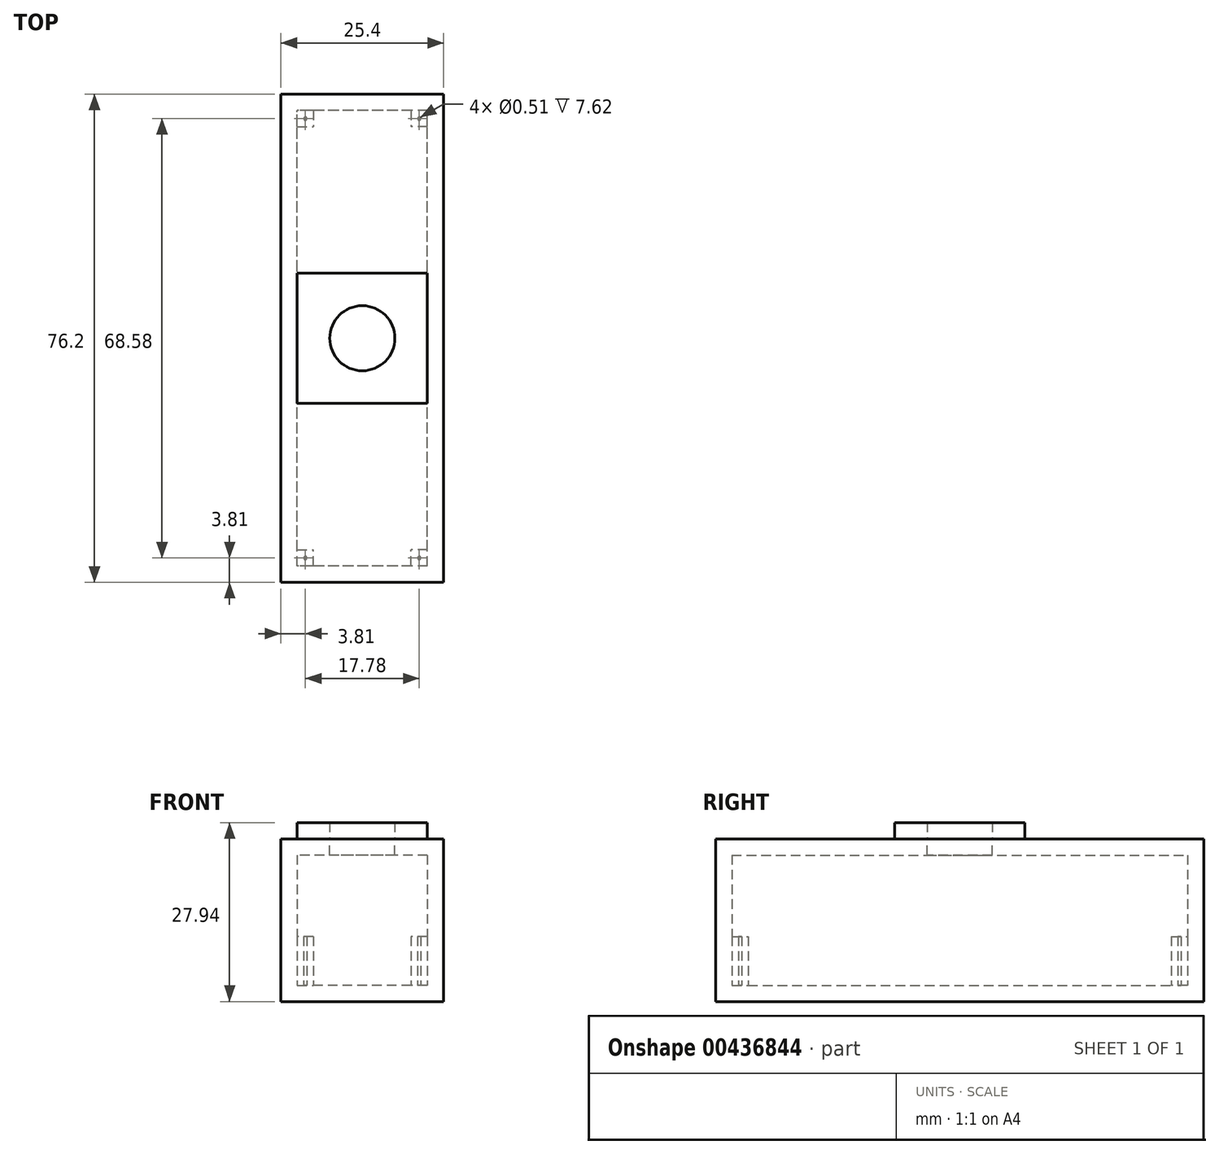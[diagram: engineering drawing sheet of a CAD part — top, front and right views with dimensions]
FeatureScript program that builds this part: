
annotation { "Feature Type Name" : "Feature", "Feature Type Description" : "" }
export const myFeature = defineFeature(function(context is Context, id is Id, definition is map)
    precondition{}
    {
        {
            var Q0;
            Q0=qCreatedBy(makeId("Front.planeOp"),FACE);
            var sketch = newSketch(context, id + "F0", { "sketchPlane" : qUnion([Q0])});
            skLineSegment(sketch, "E0.bottom", {"start": v(12.7, 12.7) * mm, "end": v(-12.7, 12.7) * mm});
            skLineSegment(sketch, "E0.top", {"start": v(12.7, -12.7) * mm, "end": v(-12.7, -12.7) * mm});
            skLineSegment(sketch, "E0.left", {"start": v(12.7, 12.7) * mm, "end": v(12.7, -12.7) * mm});
            skLineSegment(sketch, "E0.right", {"start": v(-12.7, 12.7) * mm, "end": v(-12.7, -12.7) * mm});
            skPoint(sketch, "E0.middle", {"position": v(0, 0) * mm});
            skSolve(sketch);
        }
        {
            var Q0;
            Q0=makeQuery(id+"F0.imprint","IMPRINT",FACE,{"disambiguationData":[TD([[makeQuery(id+"F0.imprint","IMPRINT",EDGE,{"derivedFrom":sQuery(id+"F0.wireOp",EDGE,"E0.bottom")}),1.0]])]});
            extrude(context, id + "F1", {"entities" : qUnion([Q0]), "endBound" : BoundingType.SYMMETRIC, "depth" : 76.2 * mm});
        }
        {
            var Q0;
            Q0=makeQuery(id+"F1.opExtrude","SWEPT_FACE",FACE,{"disambiguationData":[OSD([sQuery(id+"F0.wireOp",EDGE,"E0.right")])]});
            var Q1;
            Q1=makeQuery(id+"F1.opExtrude","SWEPT_BODY",BODY,{"disambiguationData":[OSD([sQuery(id+"F0.wireOp",EDGE,"E0.bottom"),sQuery(id+"F0.wireOp",EDGE,"E0.top"),sQuery(id+"F0.wireOp",EDGE,"E0.left"),sQuery(id+"F0.wireOp",EDGE,"E0.right")])]});
            shell(context, id + "F2", {"isHollow" : true, "entities" : qUnion([Q0]), "parts" : qUnion([Q1]), "thickness" : 2.54 * mm});
        }
        {
            var Q0;
            Q0=makeQuery(id+"F1.opExtrude","SWEPT_FACE",FACE,{"disambiguationData":[OSD([sQuery(id+"F0.wireOp",EDGE,"E0.bottom")])]});
            var sketch = newSketch(context, id + "F3", { "sketchPlane" : qUnion([Q0])});
            skLineSegment(sketch, "E1.bottom", {"start": v(10.16, 10.16) * mm, "end": v(-10.16, 10.16) * mm});
            skLineSegment(sketch, "E1.top", {"start": v(10.16, -10.16) * mm, "end": v(-10.16, -10.16) * mm});
            skLineSegment(sketch, "E1.left", {"start": v(10.16, 10.16) * mm, "end": v(10.16, -10.16) * mm});
            skLineSegment(sketch, "E1.right", {"start": v(-10.16, 10.16) * mm, "end": v(-10.16, -10.16) * mm});
            skPoint(sketch, "E1.middle", {"position": v(0, 0) * mm});
            skCircle(sketch, "E2", {"center": v(0, 0) * mm, "radius": 5.08 * mm});
            skSolve(sketch);
        }
        {
            var Q0;
            Q0=makeQuery(id+"F3.imprint","IMPRINT",FACE,{"disambiguationData":[TD([[makeQuery(id+"F3.imprint","IMPRINT",EDGE,{"derivedFrom":sQuery(id+"F3.wireOp",EDGE,"E2")}),1.0]])]});
            extrude(context, id + "F4", {"entities" : qUnion([Q0]), "operationType" : NewBodyOperationType.REMOVE, "oppositeDirection" : true, "depth" : 2.54 * mm});
        }
        {
            var Q0;
            Q0=qSketchRegion(id+"F3",true);
            extrude(context, id + "F5", {"entities" : qUnion([Q0]), "depth" : 2.54 * mm});
        }
        {
            var Q0;
            Q0=makeQuery(id+"F2.opShell","OFFSET_FACE",FACE,{"disambiguationData":[OSD([sQuery(id+"F0.wireOp",EDGE,"E0.top")])]});
            var sketch = newSketch(context, id + "F6", { "sketchPlane" : qUnion([Q0])});
            skLineSegment(sketch, "E3.bottom", {"start": v(-10.16, 35.56) * mm, "end": v(-7.62, 35.56) * mm});
            skLineSegment(sketch, "E3.top", {"start": v(-10.16, 33.02) * mm, "end": v(-7.62, 33.02) * mm});
            skLineSegment(sketch, "E3.left", {"start": v(-10.16, 35.56) * mm, "end": v(-10.16, 33.02) * mm});
            skLineSegment(sketch, "E3.right", {"start": v(-7.62, 35.56) * mm, "end": v(-7.62, 33.02) * mm});
            skLineSegment(sketch, "E4.bottom", {"start": v(10.16, 35.56) * mm, "end": v(7.62, 35.56) * mm});
            skLineSegment(sketch, "E4.top", {"start": v(10.16, 33.02) * mm, "end": v(7.62, 33.02) * mm});
            skLineSegment(sketch, "E4.left", {"start": v(10.16, 35.56) * mm, "end": v(10.16, 33.02) * mm});
            skLineSegment(sketch, "E4.right", {"start": v(7.62, 35.56) * mm, "end": v(7.62, 33.02) * mm});
            skLineSegment(sketch, "E5.bottom", {"start": v(10.16, -35.56) * mm, "end": v(7.62, -35.56) * mm});
            skLineSegment(sketch, "E5.top", {"start": v(10.16, -33.02) * mm, "end": v(7.62, -33.02) * mm});
            skLineSegment(sketch, "E5.left", {"start": v(10.16, -35.56) * mm, "end": v(10.16, -33.02) * mm});
            skLineSegment(sketch, "E5.right", {"start": v(7.62, -35.56) * mm, "end": v(7.62, -33.02) * mm});
            skLineSegment(sketch, "E6.bottom", {"start": v(-10.16, -35.56) * mm, "end": v(-7.62, -35.56) * mm});
            skLineSegment(sketch, "E6.top", {"start": v(-10.16, -33.02) * mm, "end": v(-7.62, -33.02) * mm});
            skLineSegment(sketch, "E6.left", {"start": v(-10.16, -35.56) * mm, "end": v(-10.16, -33.02) * mm});
            skLineSegment(sketch, "E6.right", {"start": v(-7.62, -35.56) * mm, "end": v(-7.62, -33.02) * mm});
            skPoint(sketch, "E7", {"position": v(-8.9, 34.3) * mm});
            skPoint(sketch, "E8", {"position": v(-8.9, -34.3) * mm});
            skPoint(sketch, "E9", {"position": v(8.9, -34.3) * mm});
            skPoint(sketch, "E10", {"position": v(8.9, 34.3) * mm});
            skCircle(sketch, "E11", {"center": v(-8.9, -34.3) * mm, "radius": 0.25 * mm});
            skCircle(sketch, "E12", {"center": v(8.9, -34.3) * mm, "radius": 0.25 * mm});
            skCircle(sketch, "E13", {"center": v(8.9, 34.3) * mm, "radius": 0.25 * mm});
            skCircle(sketch, "E14", {"center": v(-8.9, 34.3) * mm, "radius": 0.25 * mm});
            skSolve(sketch);
        }
        {
            var Q0;
            Q0=makeQuery(id+"F6.imprint","IMPRINT",FACE,{"disambiguationData":[TD([[makeQuery(id+"F6.imprint","IMPRINT",EDGE,{"derivedFrom":sQuery(id+"F6.wireOp",EDGE,"E3.bottom")}),1.0]])]});
            var Q1;
            Q1=makeQuery(id+"F6.imprint","IMPRINT",FACE,{"disambiguationData":[TD([[makeQuery(id+"F6.imprint","IMPRINT",EDGE,{"derivedFrom":sQuery(id+"F6.wireOp",EDGE,"E4.bottom")}),1.0]])]});
            var Q2;
            Q2=makeQuery(id+"F6.imprint","IMPRINT",FACE,{"disambiguationData":[TD([[makeQuery(id+"F6.imprint","IMPRINT",EDGE,{"derivedFrom":sQuery(id+"F6.wireOp",EDGE,"E5.bottom")}),-1.0]])]});
            var Q3;
            Q3=makeQuery(id+"F6.imprint","IMPRINT",FACE,{"disambiguationData":[TD([[makeQuery(id+"F6.imprint","IMPRINT",EDGE,{"derivedFrom":sQuery(id+"F6.wireOp",EDGE,"E6.bottom")}),-1.0]])]});
            extrude(context, id + "F7", {"entities" : qUnion([Q0, Q1, Q2, Q3]), "operationType" : NewBodyOperationType.ADD, "depth" : 7.62 * mm});
        }
    });
